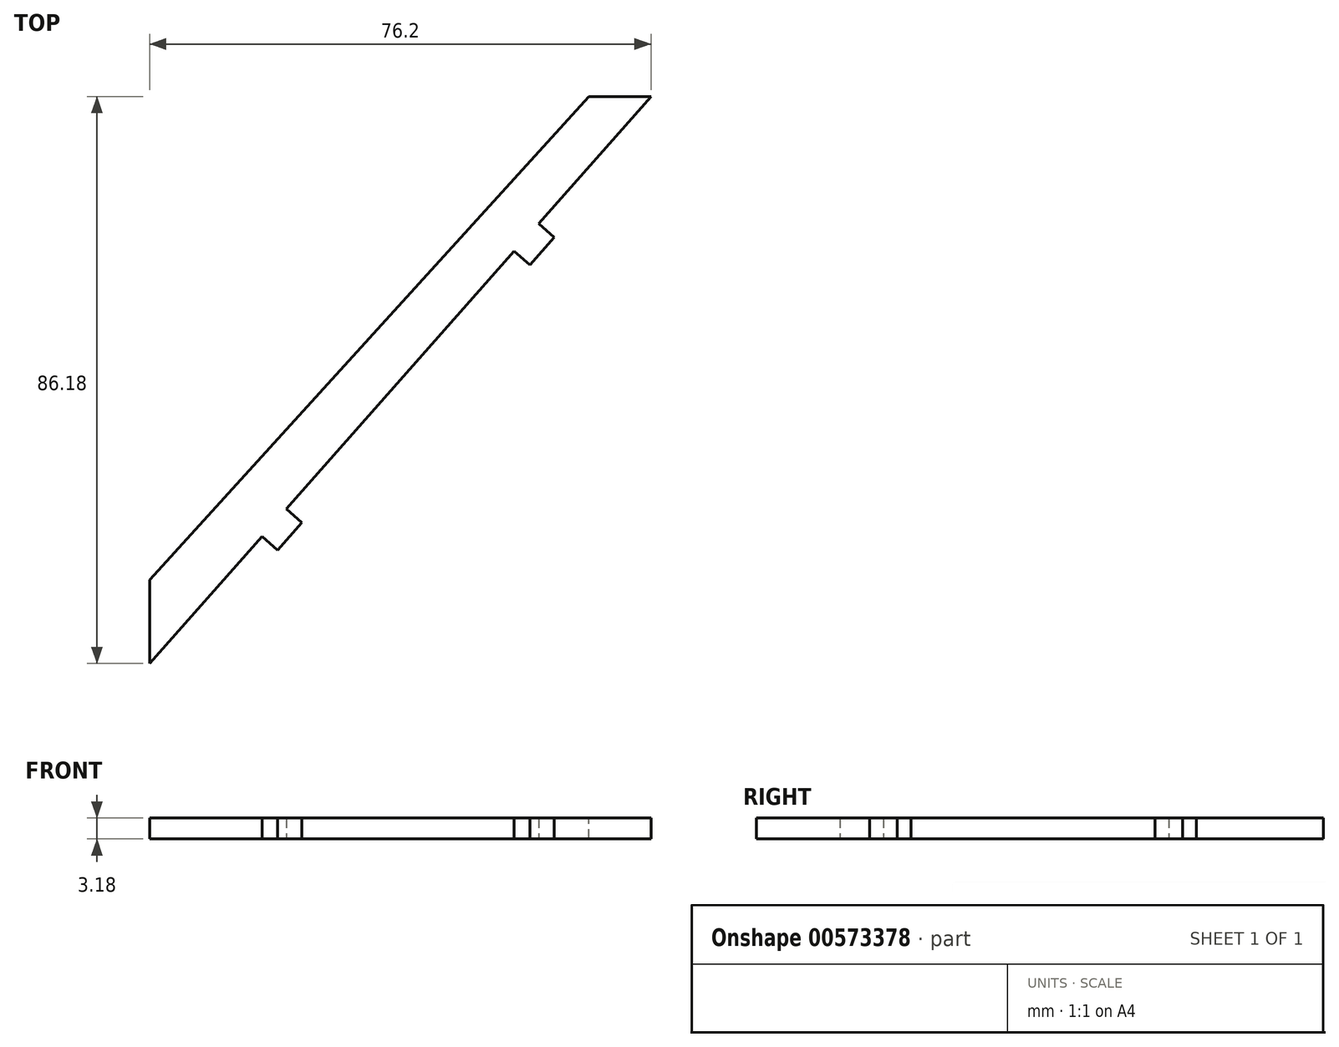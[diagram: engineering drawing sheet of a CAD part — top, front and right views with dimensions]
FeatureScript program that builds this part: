
annotation { "Feature Type Name" : "Feature", "Feature Type Description" : "" }
export const myFeature = defineFeature(function(context is Context, id is Id, definition is map)
    precondition{}
    {
        {
            var Q0;
            Q0=qCreatedBy(makeId("Top.planeOp"),FACE);
            var sketch = newSketch(context, id + "F0", { "sketchPlane" : qUnion([Q0])});
            skLineSegment(sketch, "E0", {"start": v(0, 0) * mm, "end": v(0, 86.18) * mm});
            skLineSegment(sketch, "E1", {"start": v(0, 86.18) * mm, "end": v(76.2, 86.18) * mm});
            skLineSegment(sketch, "E2", {"start": v(59.65, 62.67) * mm, "end": v(57.63, 60.39) * mm});
            skLineSegment(sketch, "E3", {"start": v(20.78, 23.5) * mm, "end": v(55.42, 62.68) * mm});
            skLineSegment(sketch, "E4", {"start": v(76.2, 86.18) * mm, "end": v(59.12, 66.87) * mm});
            skLineSegment(sketch, "E5", {"start": v(19.46, 17.21) * mm, "end": v(23.16, 21.4) * mm});
            skLineSegment(sketch, "E6", {"start": v(23.16, 21.4) * mm, "end": v(20.78, 23.5) * mm});
            skLineSegment(sketch, "E7", {"start": v(19.46, 17.21) * mm, "end": v(17.08, 19.31) * mm});
            skLineSegment(sketch, "E8", {"start": v(17.08, 19.31) * mm, "end": v(0, 0) * mm});
            skLineSegment(sketch, "E9", {"start": v(57.8, 60.58) * mm, "end": v(61.5, 64.76) * mm});
            skLineSegment(sketch, "E10", {"start": v(61.5, 64.76) * mm, "end": v(59.12, 66.87) * mm});
            skLineSegment(sketch, "E11", {"start": v(57.8, 60.58) * mm, "end": v(55.42, 62.68) * mm});
            skSolve(sketch);
        }
        {
            var Q0;
            Q0 = qSketchRegion(id + "F0", true);
            extrude(context, id + "F1", {"entities" : qUnion([Q0]), "depth" : 3.17 * mm, "offsetDistance" : 25.4 * mm});
        }
        {
            var Q0;
            Q0=qCreatedBy(makeId("Top.planeOp"),FACE);
            var sketch = newSketch(context, id + "F2", { "sketchPlane" : qUnion([Q0])});
            skLineSegment(sketch, "E12", {"start": v(0, 0) * mm, "end": v(0, 12.7) * mm});
            skLineSegment(sketch, "E13", {"start": v(0, 12.7) * mm, "end": v(71.23, 91.08) * mm});
            skLineSegment(sketch, "E14", {"start": v(71.23, 91.08) * mm, "end": v(0, 91.08) * mm});
            skLineSegment(sketch, "E15", {"start": v(0, 91.08) * mm, "end": v(0, 12.7) * mm});
            skSolve(sketch);
        }
        {
            var Q0;
            Q0 = qSketchRegion(id + "F2", true);
            extrude(context, id + "F3", {"entities" : qUnion([Q0]), "operationType" : NewBodyOperationType.REMOVE, "depth" : 25.4 * mm, "offsetDistance" : 25.4 * mm});
        }
    });
